# Revit family: Offset_Tube_Chutes
name_source: partatom
category: Specialty Equipment
units: mm (PartAtom-declared; Revit-internal decimal feet)

## family parameters
Always vertical = No
Classification Number = 23.15.30.21.14
Cut with Voids When Loaded = No
Enable Cutting in Views = No
Maintain Annotation Orientation = No
Part Type = Normal
Room Calculation Point = No
Round Connector Dimension = Use Diameter
Shared = No
Work Plane-Based = No

## types (4) — shared parameters
Assembly Code = D1090510
Construction Details = http://www.arcat.com
Default Elevation = 0' - 0"
Green Building-LEED = http://www.arcat.com
Height = 0' - 0"
Installation_Fabricaton = http://www.chutes.com
Keynote = 14 91 00
Manufacturer = CHUTES International
Manufacturer Fax = 301-753-4108
Manufacturer Website = http://www.chutes.com
Material = Mirror Finish Aluminum
Product Data = http://www.arcat.com
Product Properties = http://www.arcat.com
Sales Information = http://www.chutes.com
Send Message = http://www.arcat.com
Specification = http://www.arcat.com
URL = http://www.chutes.com
Width = 0' - 0"
zero-valued in all types: Expected Lifespan (Years), Maintenance Schedule (Months), Warranty Duration (Years)

## per-type parameters (varying)
| type | Description | Diameter | Model |
| 24" Diameter | 24" Diameter Offset Chute as Specified in 14 91 00 | 2' - 0" | 24" Diameter Offset Chute |
| 28" Diameter | 28" Diameter Offset Chute as Specified in 14 91 00 | 2' - 4" | 28" Diameter Offset Chute |
| 30" Diameter | 30" Diameter Offset Chute as Specified in 14 91 00 | 2' - 6" | 30" Diameter Offset Chute |
| 36" Diameter | 36" Diameter Offset Chute as Specified in 14 91 00 | 3' - 0" | 36" Diameter Offset Chute |

## geometry (parser evidence)
native form markers: Blend x6, Sweep x3
no freeform markers — native parametric forms only
